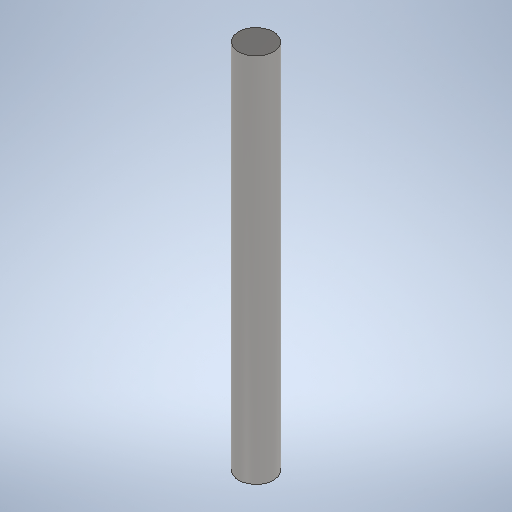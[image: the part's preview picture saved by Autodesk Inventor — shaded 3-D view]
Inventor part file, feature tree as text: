
AUTODESK INVENTOR PART (.ipt)
format: ipt  version: 2025.1 (Build 291241000, 241)  size: 229,376 bytes
history: native  units: mm
features: extrude x1, sketch x1
ambient origin geometry x8: Origin, YZ Plane, XZ Plane, XY Plane, X Axis, Y Axis, Z Axis, Center Point
bodies: Solid1 (feature_tree)
feature tree (2):
  extrude  "Extrusion1"  TaperAngle=0.0deg  [1 undecoded]
  sketch  "Sketch1"  dims[d0=8.0mm d2=0.0mm]
note: 1 required parameter value undecoded (feature->parameter linkage not recoverable at this tier; creation-order binding heuristic only, values carry confidence <= 0.55)
